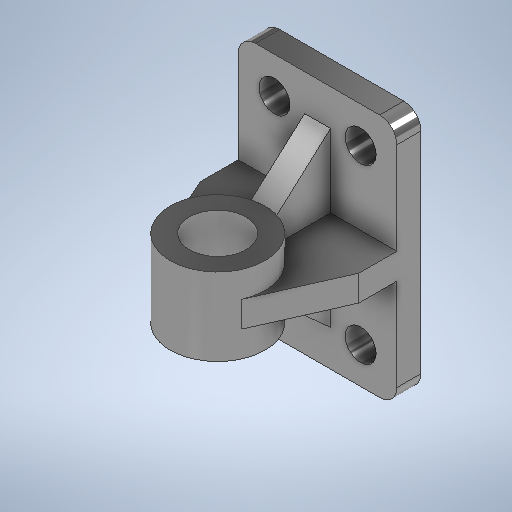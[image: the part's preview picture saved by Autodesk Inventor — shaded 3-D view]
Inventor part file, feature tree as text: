
AUTODESK INVENTOR PART (.ipt)
format: ipt  version: 2025.2 (Build 292293000, 293)  size: 1,893,376 bytes
history: native  units: in
note: dims shown in document units (in); Inventor stores cm internally (conversion verified against a paired STEP export)
features: sketch x10, extrude x4, rib x1, plane x1, mirror x1, other x1
ambient origin geometry x8: Origin, YZ Plane, XZ Plane, XY Plane, X Axis, Y Axis, Z Axis, Center Point
bodies: Solid1 (feature_tree)
feature tree (18):
  extrude  "Extrusion1"  Depth=0.7874in
  extrude  "Extrusion2"  Depth=0.3937in
  sketch  "Sketch3"  dims[d27=0.8268in d28=0.5512in d29=0.0in]
  extrude  "Extrusion3"  Depth=0.3937in
  extrude  "Extrusion4"  Depth=0.5512in TaperAngle=0.0deg
  sketch  "Sketch6"  dims[d37=2.1654in]
  sketch  "Sketch7"  dims[d38=0.8661in]
  sketch  "Sketch8"  dims[d39=0.8661in]
  rib  "Rib1"
  plane  "Work Plane1"
  mirror  "Mirror1"
  sketch  "Sketch1"  dims[d9=0.7087in d13=0.7874in d15=1.9685in d16=0.7874in d18=3.937in]
  other  "Image1"
  sketch  "Sketch Rectangular Pattern1"  dims[d23=0.3937in d24=0.3937in]
  sketch  "Sketch2"  dims[d25=0.3937in d26=0.8268in]
  sketch  "Sketch4"  dims[d33=1.7717in d34=0.0in]
  sketch  "Sketch5"  dims[d36=2.2835in]
  sketch  "Sketch9"  dims[d40=0.5906in d41=0.0in d42=2.1654in d43=1.2992in d44=1.7717in d45=0.0in d46=0.0394in d47=0.5906in d48=0.0in d49=0.0in d50=0.0394in d51=0.0394in d22=0.0197in]
